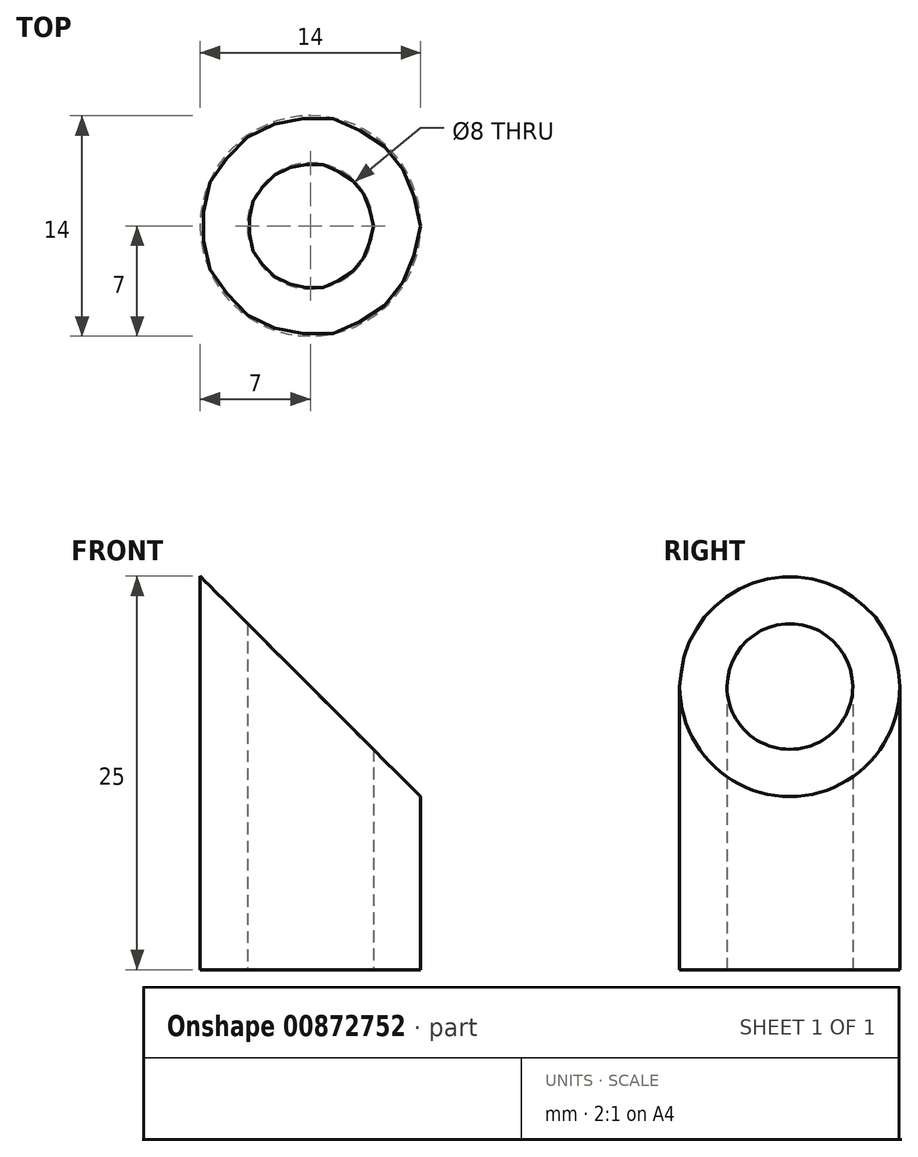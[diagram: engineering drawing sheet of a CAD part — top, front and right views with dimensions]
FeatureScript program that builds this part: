
annotation { "Feature Type Name" : "Feature", "Feature Type Description" : "" }
export const myFeature = defineFeature(function(context is Context, id is Id, definition is map)
    precondition{}
    {
        {
            var Q0;
            Q0=qCreatedBy(makeId("Top.planeOp"),FACE);
            var sketch = newSketch(context, id + "F0", { "sketchPlane" : qUnion([Q0])});
            skCircle(sketch, "E0", {"center": v(0, 0) * mm, "radius": 7 * mm});
            skCircle(sketch, "E1", {"center": v(0, 0) * mm, "radius": 4 * mm});
            skSolve(sketch);
        }
        {
            var Q0;
            Q0=makeQuery(id+"F0.imprint","IMPRINT",FACE,{"disambiguationData":[TD([[makeQuery(id+"F0.imprint","IMPRINT",EDGE,{"derivedFrom":sQuery(id+"F0.wireOp",EDGE,"E0")}),1.0]])]});
            extrude(context, id + "F1", {"entities" : qUnion([Q0]), "depth" : 25 * mm, "offsetDistance" : 25 * mm});
        }
        {
            var Q0;
            Q0=qCreatedBy(makeId("Front.planeOp"),FACE);
            var sketch = newSketch(context, id + "F2", { "sketchPlane" : qUnion([Q0])});
            skLineSegment(sketch, "E2", {"start": v(7, 25) * mm, "end": v(7, 0) * mm});
            skLineSegment(sketch, "E3", {"start": v(-7, 0) * mm, "end": v(-7, 25) * mm});
            skLineSegment(sketch, "E4", {"start": v(-7, 25) * mm, "end": v(7, 11) * mm});
            skLineSegment(sketch, "E5", {"start": v(-7, 25) * mm, "end": v(7, 25) * mm});
            skSolve(sketch);
        }
        {
            var Q0;
            {var subQ2=sQuery(id+"F2.wireOp",EDGE,"E4");Q0=makeQuery(id+"F2.imprint","IMPRINT",FACE,{"disambiguationData":[TD([[makeQuery(id+"F2.imprint","IMPRINT",EDGE,{"derivedFrom":subQ2}),1.0]])]});}
            extrude(context, id + "F3", {"entities" : qUnion([Q0]), "operationType" : NewBodyOperationType.REMOVE, "oppositeDirection" : true, "depth" : 25 * mm, "offsetDistance" : 25 * mm, "symmetric" : true});
        }
    });
